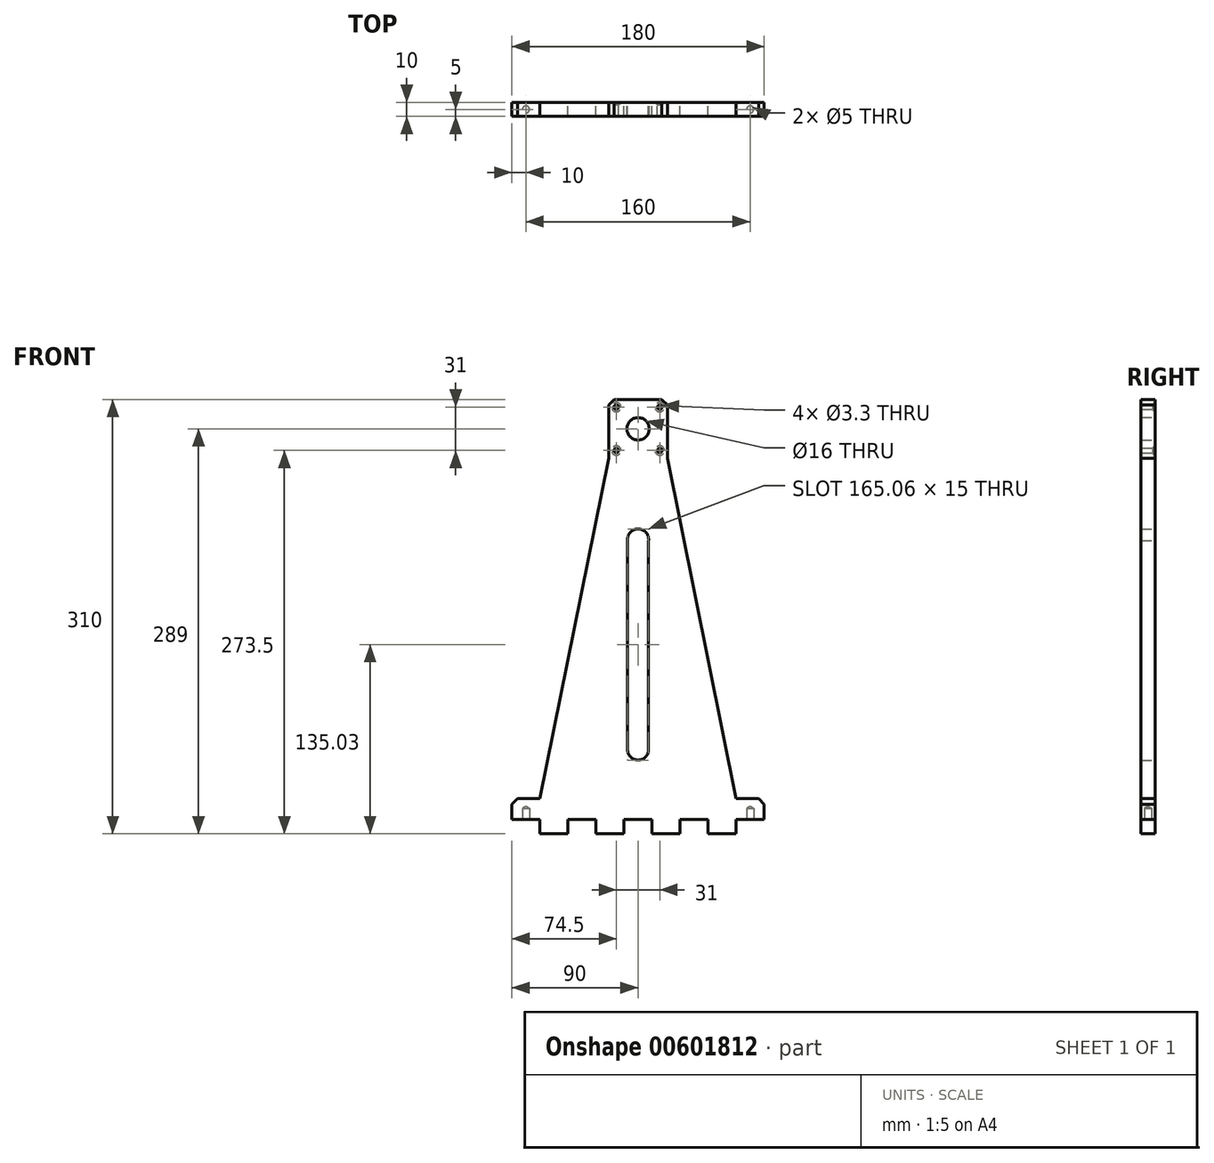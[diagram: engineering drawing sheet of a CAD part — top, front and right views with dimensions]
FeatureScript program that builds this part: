
annotation { "Feature Type Name" : "Feature", "Feature Type Description" : "" }
export const myFeature = defineFeature(function(context is Context, id is Id, definition is map)
    precondition{}
    {
        {
            var Q0;
            Q0=qCreatedBy(makeId("Front.planeOp"),FACE);
            var sketch = newSketch(context, id + "F0", { "sketchPlane" : qUnion([Q0])});
            skLineSegment(sketch, "E0.bottom", {"start": v(0, 0) * mm, "end": v(-10, 0) * mm});
            skLineSegment(sketch, "E0.left", {"start": v(0, 0) * mm, "end": v(0, 300) * mm, "construction": true});
            skLineSegment(sketch, "E1", {"start": v(-90, 0) * mm, "end": v(-90, 15) * mm});
            skLineSegment(sketch, "E2", {"start": v(-90, 15) * mm, "end": v(-70, 15) * mm});
            skLineSegment(sketch, "E3", {"start": v(-70, 15) * mm, "end": v(-21, 258) * mm});
            skLineSegment(sketch, "E4", {"start": v(-21, 258) * mm, "end": v(-21, 300) * mm});
            skLineSegment(sketch, "E5", {"start": v(-21, 300) * mm, "end": v(0, 300) * mm});
            skLineSegment(sketch, "E6", {"start": v(-21, 279) * mm, "end": v(0, 279) * mm, "construction": true});
            skLineSegment(sketch, "E7.bottom", {"start": v(15.5, 294.5) * mm, "end": v(-15.5, 294.5) * mm, "construction": true});
            skLineSegment(sketch, "E7.top", {"start": v(15.5, 263.5) * mm, "end": v(-15.5, 263.5) * mm, "construction": true});
            skLineSegment(sketch, "E7.left", {"start": v(15.5, 294.5) * mm, "end": v(15.5, 263.5) * mm, "construction": true});
            skLineSegment(sketch, "E7.right", {"start": v(-15.5, 294.5) * mm, "end": v(-15.5, 263.5) * mm, "construction": true});
            skPoint(sketch, "E7.middle", {"position": v(0, 279) * mm});
            skArc(sketch, "E8", {"start": v(-7.5, 50) * mm, "mid": v(0, 42.5) * mm, "end": v(7.5, 50) * mm});
            skArc(sketch, "E9", {"start": v(7.5, 199.05) * mm, "mid": v(0, 207.56) * mm, "end": v(-7.5, 199.05) * mm});
            skLineSegment(sketch, "E10", {"start": v(7.5, 50) * mm, "end": v(7.5, 199.05) * mm});
            skLineSegment(sketch, "E11.MirrorCS", {"start": v(-7.5, 50) * mm, "end": v(-7.5, 199.05) * mm});
            skLineSegment(sketch, "E12.MirrorCS", {"start": v(0, 0) * mm, "end": v(10, 0) * mm});
            skLineSegment(sketch, "E13.MirrorCS", {"start": v(90, 0) * mm, "end": v(90, 15) * mm});
            skLineSegment(sketch, "E14.MirrorCS", {"start": v(90, 15) * mm, "end": v(70, 15) * mm});
            skLineSegment(sketch, "E15.MirrorCS", {"start": v(70, 15) * mm, "end": v(21, 258) * mm});
            skLineSegment(sketch, "E16.MirrorCS", {"start": v(21, 258) * mm, "end": v(21, 300) * mm});
            skLineSegment(sketch, "E17.MirrorCS", {"start": v(21, 300) * mm, "end": v(0, 300) * mm});
            skCircle(sketch, "E18", {"center": v(0, 279) * mm, "radius": 8 * mm});
            skLineSegment(sketch, "E19", {"start": v(-70, 0) * mm, "end": v(-70, -10) * mm});
            skLineSegment(sketch, "E20", {"start": v(-70, -10) * mm, "end": v(-50, -10) * mm});
            skLineSegment(sketch, "E21", {"start": v(-50, -10) * mm, "end": v(-50, 0) * mm});
            skLineSegment(sketch, "E22", {"start": v(-30, 0) * mm, "end": v(-30, -10) * mm});
            skLineSegment(sketch, "E23", {"start": v(-30, -10) * mm, "end": v(-10, -10) * mm});
            skLineSegment(sketch, "E24", {"start": v(-10, -10) * mm, "end": v(-10, 0) * mm});
            skLineSegment(sketch, "E25.MirrorCS", {"start": v(70, 0) * mm, "end": v(70, -10) * mm});
            skLineSegment(sketch, "E26.MirrorCS", {"start": v(70, -10) * mm, "end": v(50, -10) * mm});
            skLineSegment(sketch, "E27.MirrorCS", {"start": v(50, -10) * mm, "end": v(50, 0) * mm});
            skLineSegment(sketch, "E28.MirrorCS", {"start": v(30, 0) * mm, "end": v(30, -10) * mm});
            skLineSegment(sketch, "E29.MirrorCS", {"start": v(30, -10) * mm, "end": v(10, -10) * mm});
            skLineSegment(sketch, "E30.MirrorCS", {"start": v(10, -10) * mm, "end": v(10, 0) * mm});
            skLineSegment(sketch, "E31.trimOffspring", {"start": v(-70, 0) * mm, "end": v(-90, 0) * mm});
            skLineSegment(sketch, "E32.trimOffspring", {"start": v(-30, 0) * mm, "end": v(-50, 0) * mm});
            skLineSegment(sketch, "E33.trimOffspring", {"start": v(30, 0) * mm, "end": v(50, 0) * mm});
            skLineSegment(sketch, "E34.trimOffspring", {"start": v(70, 0) * mm, "end": v(90, 0) * mm});
            skSolve(sketch);
        }
        {
            var Q0;
            Q0=makeQuery(id+"F0.imprint","IMPRINT",FACE,{"disambiguationData":[TD([[makeQuery(id+"F0.imprint","IMPRINT",EDGE,{"derivedFrom":sQuery(id+"F0.wireOp",EDGE,"E0.bottom")}),-1.0]])]});
            extrude(context, id + "F1", {"entities" : qUnion([Q0]), "depth" : 10 * mm, "offsetDistance" : 25 * mm});
        }
        {
            var Q0;
            Q0=makeQuery(id+"F1.opExtrude","SWEPT_EDGE",EDGE,{"disambiguationData":[OSD([sQuery(id+"F0.wireOp",EDGE,"E16.MirrorCS"),sQuery(id+"F0.wireOp",EDGE,"E17.MirrorCS")])]});
            var Q1;
            Q1=makeQuery(id+"F1.opExtrude","SWEPT_EDGE",EDGE,{"disambiguationData":[OSD([sQuery(id+"F0.wireOp",EDGE,"E4"),sQuery(id+"F0.wireOp",EDGE,"E5")])]});
            chamfer(context, id + "F2", {"entities" : qUnion([Q0, Q1]), "width" : 4 * mm, "tangentPropagation" : true});
        }
        {
            var Q0;
            Q0=makeQuery(id+"F1.opExtrude","SWEPT_EDGE",EDGE,{"disambiguationData":[OSD([sQuery(id+"F0.wireOp",EDGE,"E1"),sQuery(id+"F0.wireOp",EDGE,"E2")])]});
            var Q1;
            Q1=makeQuery(id+"F1.opExtrude","SWEPT_EDGE",EDGE,{"disambiguationData":[OSD([sQuery(id+"F0.wireOp",EDGE,"E13.MirrorCS"),sQuery(id+"F0.wireOp",EDGE,"E14.MirrorCS")])]});
            chamfer(context, id + "F3", {"entities" : qUnion([Q0, Q1]), "width" : 4 * mm, "tangentPropagation" : true});
        }
        {
            var Q0;
            Q0=sQuery(id+"F0.wireOp",VERTEX,"E7.right.start");
            var Q1;
            Q1=sQuery(id+"F0.wireOp",VERTEX,"E7.bottom.start");
            var Q2;
            Q2=sQuery(id+"F0.wireOp",VERTEX,"E7.top.start");
            var Q3;
            Q3=sQuery(id+"F0.wireOp",VERTEX,"E7.right.end");
            var Q4;
            Q4=makeQuery(id+"F1.opExtrude","SWEPT_BODY",BODY,{"disambiguationData":[OSD([sQuery(id+"F0.wireOp",EDGE,"E0.bottom"),sQuery(id+"F0.wireOp",EDGE,"E1"),sQuery(id+"F0.wireOp",EDGE,"E2"),sQuery(id+"F0.wireOp",EDGE,"E3"),sQuery(id+"F0.wireOp",EDGE,"E4"),sQuery(id+"F0.wireOp",EDGE,"E5"),sQuery(id+"F0.wireOp",EDGE,"E8"),sQuery(id+"F0.wireOp",EDGE,"E9"),sQuery(id+"F0.wireOp",EDGE,"E10"),sQuery(id+"F0.wireOp",EDGE,"E11.MirrorCS"),sQuery(id+"F0.wireOp",EDGE,"E12.MirrorCS"),sQuery(id+"F0.wireOp",EDGE,"E13.MirrorCS"),sQuery(id+"F0.wireOp",EDGE,"E14.MirrorCS"),sQuery(id+"F0.wireOp",EDGE,"E15.MirrorCS"),sQuery(id+"F0.wireOp",EDGE,"E16.MirrorCS"),sQuery(id+"F0.wireOp",EDGE,"E17.MirrorCS")])]});
            hole(context, id + "F4", {"style" : HoleStyle.C_SINK, "endStyle" : HoleEndStyle.THROUGH, "oppositeDirection" : true, "standardTappedOrClearance" : lookupTablePath({ "standard" : "ISO", "fit" : "Normal", "size" : "M3", "type" : "Clearance" }), "standardBlindInLast" : lookupTablePath({ "fit" : "Standard", "standard" : "ISO", "size" : "M3", "type" : "Clearance" }), "holeDiameter" : 3.3 * mm, "cSinkDiameter" : 6.72 * mm, "cSinkAngle" : 90 * degree, "majorDiameter" : 5 * mm, "isTappedThrough" : true, "tappedDepth" : 12 * mm, "tapClearance" : 3, "locations" : qUnion([Q0, Q1, Q2, Q3]), "scope" : qUnion([Q4])});
        }
        {
            var Q0;
            Q0=makeQuery(id+"F1.opExtrude","SWEPT_FACE",FACE,{"disambiguationData":[OSD([sQuery(id+"F0.wireOp",EDGE,"E31.trimOffspring")])]});
            var sketch = newSketch(context, id + "F5", { "sketchPlane" : qUnion([Q0])});
            skPoint(sketch, "E35", {"position": v(-80, 5) * mm});
            skPoint(sketch, "E35.positionSnap0", {"position": v(-90, 5) * mm});
            skPoint(sketch, "E36", {"position": v(80, 5) * mm});
            skSolve(sketch);
        }
        {
            var Q0;
            Q0=sQuery(id+"F5.wireOp",VERTEX,"E35");
            var Q1;
            Q1=sQuery(id+"F5.wireOp",VERTEX,"E36");
            var Q2;
            Q2=makeQuery(id+"F1.opExtrude","SWEPT_BODY",BODY,{"disambiguationData":[OSD([sQuery(id+"F0.wireOp",EDGE,"E0.bottom"),sQuery(id+"F0.wireOp",EDGE,"E1"),sQuery(id+"F0.wireOp",EDGE,"E2"),sQuery(id+"F0.wireOp",EDGE,"E3"),sQuery(id+"F0.wireOp",EDGE,"E4"),sQuery(id+"F0.wireOp",EDGE,"E5"),sQuery(id+"F0.wireOp",EDGE,"E8"),sQuery(id+"F0.wireOp",EDGE,"E9"),sQuery(id+"F0.wireOp",EDGE,"E10"),sQuery(id+"F0.wireOp",EDGE,"E11.MirrorCS"),sQuery(id+"F0.wireOp",EDGE,"E12.MirrorCS"),sQuery(id+"F0.wireOp",EDGE,"E13.MirrorCS"),sQuery(id+"F0.wireOp",EDGE,"E14.MirrorCS"),sQuery(id+"F0.wireOp",EDGE,"E15.MirrorCS"),sQuery(id+"F0.wireOp",EDGE,"E16.MirrorCS"),sQuery(id+"F0.wireOp",EDGE,"E17.MirrorCS"),sQuery(id+"F0.wireOp",EDGE,"E18"),sQuery(id+"F0.wireOp",EDGE,"E19"),sQuery(id+"F0.wireOp",EDGE,"E20"),sQuery(id+"F0.wireOp",EDGE,"E21"),sQuery(id+"F0.wireOp",EDGE,"E22"),sQuery(id+"F0.wireOp",EDGE,"E23"),sQuery(id+"F0.wireOp",EDGE,"E24"),sQuery(id+"F0.wireOp",EDGE,"E25.MirrorCS"),sQuery(id+"F0.wireOp",EDGE,"E26.MirrorCS"),sQuery(id+"F0.wireOp",EDGE,"E27.MirrorCS"),sQuery(id+"F0.wireOp",EDGE,"E28.MirrorCS"),sQuery(id+"F0.wireOp",EDGE,"E29.MirrorCS"),sQuery(id+"F0.wireOp",EDGE,"E30.MirrorCS"),sQuery(id+"F0.wireOp",EDGE,"E31.trimOffspring"),sQuery(id+"F0.wireOp",EDGE,"E32.trimOffspring"),sQuery(id+"F0.wireOp",EDGE,"E33.trimOffspring"),sQuery(id+"F0.wireOp",EDGE,"E34.trimOffspring")])]});
            hole(context, id + "F6", {"style" : HoleStyle.SIMPLE, "endStyle" : HoleEndStyle.BLIND, "standardTappedOrClearance" : lookupTablePath({ "standard" : "ISO", "engagement" : "75%", "pitch" : "1 mm", "size" : "M6", "type" : "Tapped" }), "standardBlindInLast" : lookupTablePath({ "standard" : "ISO", "engagement" : "75%", "pitch" : "1 mm", "size" : "M6", "type" : "Tapped" }), "holeDiameter" : 5 * mm, "majorDiameter" : 6 * mm, "showTappedDepth" : true, "holeDepth" : 8 * mm, "isTappedThrough" : true, "tappedDepth" : 5 * mm, "tapClearance" : 3, "locations" : qUnion([Q0, Q1]), "scope" : qUnion([Q2])});
        }
    });
